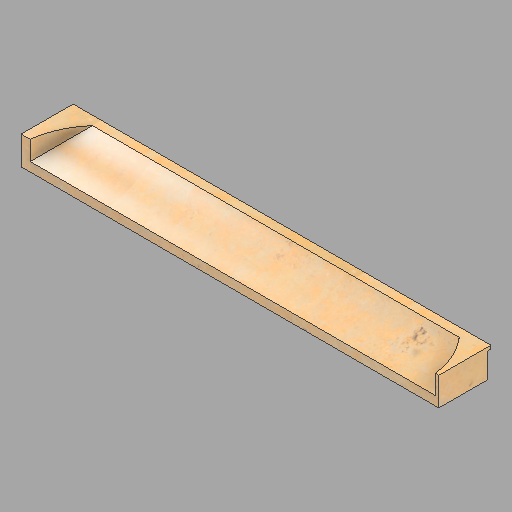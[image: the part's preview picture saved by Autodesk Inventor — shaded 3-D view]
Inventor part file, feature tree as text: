
AUTODESK INVENTOR PART (.ipt)
format: ipt  version: 2022.2 (Build 262287010, 287A)  size: 210,944 bytes
history: native  units: in
note: dims shown in document units (in); Inventor stores cm internally (conversion verified against a paired STEP export)
features: revolve x2, other x1, direct_edit x1
ambient origin geometry x8: Origin, YZ Plane, XZ Plane, XY Plane, X Axis, Y Axis, Z Axis, Center Point
bodies: Solid1 (feature_tree)
feature tree (4):
  other  "Head (R)"
  direct_edit  "Direct Edit1"
  revolve  "Rotate1"  Angle=180.0deg
  revolve  "Rotate2"  [1 undecoded]
note: 1 required parameter value undecoded (feature->parameter linkage not recoverable at this tier; creation-order binding heuristic only, values carry confidence <= 0.55)
